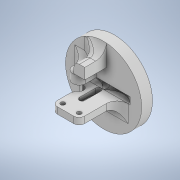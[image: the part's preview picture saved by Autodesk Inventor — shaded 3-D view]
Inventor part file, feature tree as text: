
AUTODESK INVENTOR PART (.ipt)
format: ipt  version: 2021 (Build 250183000, 183)  size: 372,736 bytes
history: native  units: mm
features: extrude x12, sketch x12, fillet x7, other x5, reference x2, projected_geometry x2
ambient origin geometry x8: Origin, YZ Plane, XZ Plane, XY Plane, X Axis, Y Axis, Z Axis, Center Point
bodies: Solid1 (feature_tree)
feature tree (40):
  extrude  "Extrusion1"  Depth=10.0mm TaperAngle=0.0deg
  extrude  "Extrusion2"  Depth=3.6mm TaperAngle=0.0deg
  extrude  "Extrusion3"  Depth=3.6mm TaperAngle=0.0deg
  extrude  "Extrusion4"  Depth=39.0mm
  fillet  "Fillet1"  Radius=2.7mm
  fillet  "Fillet2"  Radius=3.0mm
  extrude  "Extrusion5"  Depth=10.0mm
  extrude  "Extrusion6"  Depth=20.0mm TaperAngle=0.0deg
  extrude  "Extrusion7"  Depth=5.0mm
  fillet  "Fillet3"  Radius=20.0mm
  extrude  "Extrusion8"  Depth=3.0mm
  extrude  "Extrusion9"  Depth=3.6mm
  extrude  "Extrusion10"  Depth=10.0mm
  fillet  "Fillet4"  Radius=10.0mm
  fillet  "Fillet5"  Radius=8.0mm
  extrude  "Extrusion11"  Depth=10.0mm
  fillet  "Fillet6"  Radius=25.0mm
  extrude  "Extrusion12"  Depth=2.5mm
  fillet  "Fillet7"  Radius=12.5mm
  sketch  "Sketch1"  dims[d0=70.0mm d1=10.0mm d2=0.0mm]
  sketch  "Sketch2"  dims[d3=21.0mm d4=3.6mm d5=0.0mm]
  sketch  "Sketch3"  dims[d6=6.0mm d7=3.6mm d8=0.0mm]
  sketch  "Sketch4"  dims[d9=40.5mm d10=39.0mm d11=2.7mm d12=3.0mm]
  sketch  "Sketch5"  dims[d13=10.0mm d14=10.0mm]
  sketch  "Sketch6"  dims[d15=12.5mm d16=20.0mm d17=0.0mm]
  reference  "Reference1"
  sketch  "Sketch7"  dims[d18=10.0mm d19=5.0mm d20=20.0mm]
  projected_geometry  "Projected Loop1"
  sketch  "Sketch8"  dims[d21=8.0mm d22=3.0mm]
  sketch  "Sketch9"  dims[d23=20.0mm d24=0.0mm d25=3.6mm]
  sketch  "Sketch10"  dims[d26=10.0mm d27=0.0mm d28=12.0mm d29=10.0mm d30=0.0mm d31=8.0mm]
  sketch  "Sketch11"  dims[d32=31.0mm d33=20.0mm d35=25.0mm d36=10.0mm d38=10.0mm]
  reference  "Reference2"
  sketch  "Sketch13"  dims[d40=3.0mm d41=3.4mm d42=0.0mm d43=0.0mm d44=25.0mm d45=6.0mm d46=12.5mm d47=35.0mm d48=0.0mm d49=4.0mm d50=4.0mm d51=5.0mm d52=5.0mm d53=5.0mm d54=5.0mm d55=45.0mm d56=0.0mm d57=5.0mm d58=10.0mm d59=8.0mm d60=1.0mm d61=0.0mm d62=6.0mm d63=0.0mm d64=8.0mm d65=5.0mm d66=20.0mm d67=0.0mm d68=2.5mm d69=7.0mm d70=0.0mm d71=6.0mm d72=0.0mm d73=2.5mm]
  projected_geometry  "Projected Loop2"
  parser-record x1  (decoder bookkeeping rows leaked as tree rows — omitted from the tree; the rows remain in map.json)
  other  "Złożenie gripper.iam"
  other  "przekładnia gripper:1"
  other  "Spur Gears:1"
  other  "Spur Gear2:1"
note: 1 file-system path scrubbed to <path> (originals preserved in map.json)
